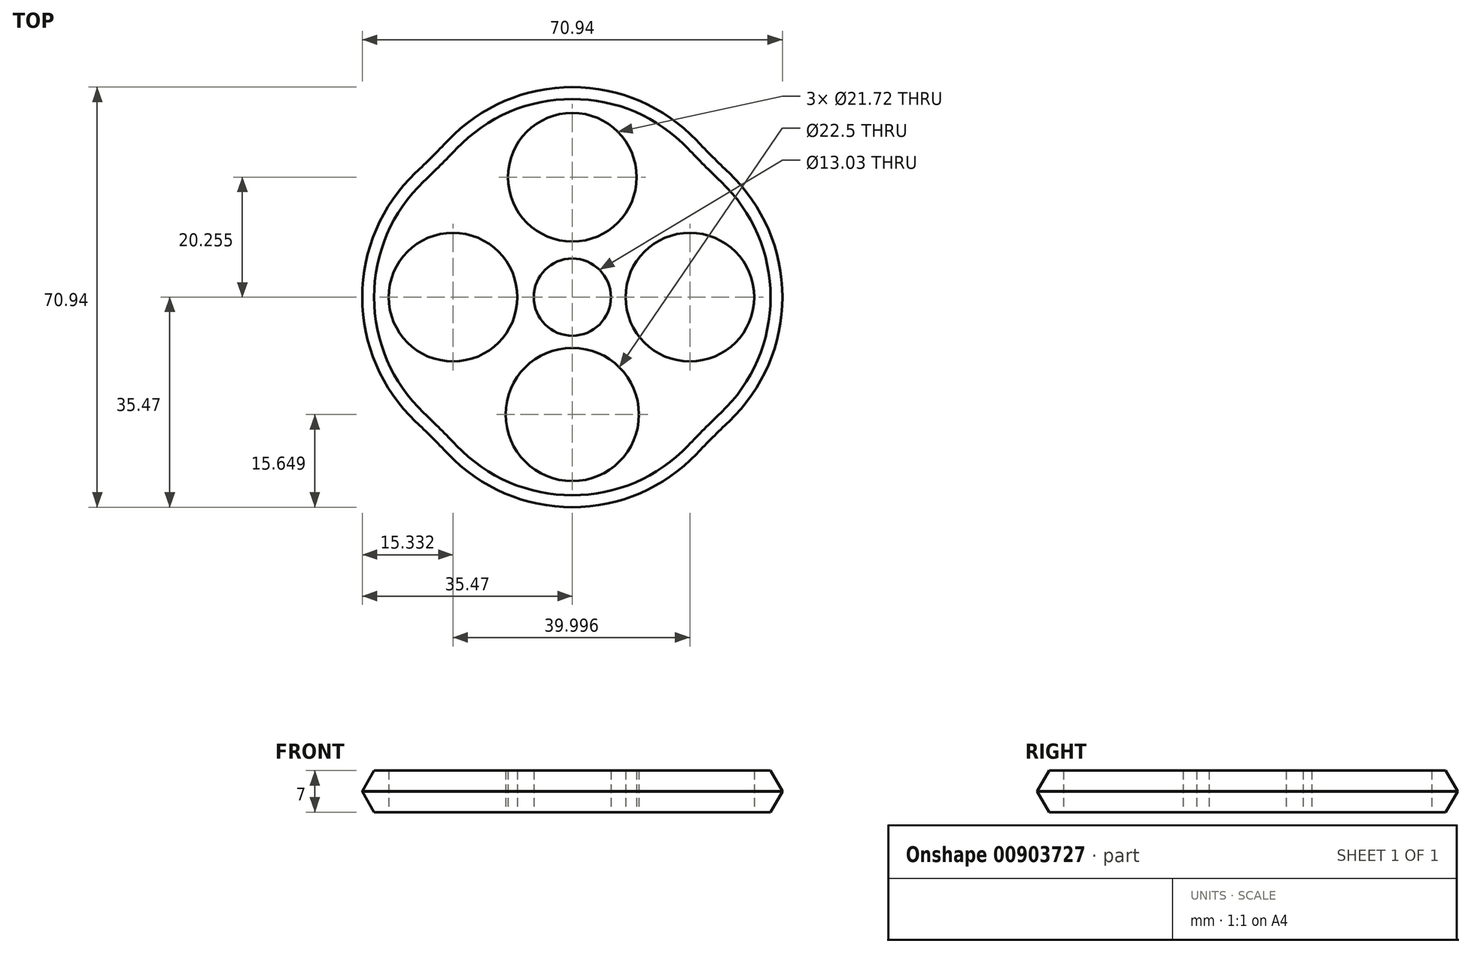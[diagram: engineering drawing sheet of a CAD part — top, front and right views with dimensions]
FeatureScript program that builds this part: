
annotation { "Feature Type Name" : "Feature", "Feature Type Description" : "" }
export const myFeature = defineFeature(function(context is Context, id is Id, definition is map)
    precondition{}
    {
        {
            var Q0;
            Q0=qCreatedBy(makeId("Top.planeOp"),FACE);
            var sketch = newSketch(context, id + "F0", { "sketchPlane" : qUnion([Q0])});
            skCircle(sketch, "E0", {"center": v(0, 0) * mm, "radius": 6.51 * mm});
            skCircle(sketch, "E1", {"center": v(0, 6.51) * mm, "radius": 28.95 * mm});
            skCircle(sketch, "E2", {"center": v(0, -6.51) * mm, "radius": 28.95 * mm});
            skCircle(sketch, "E3", {"center": v(-6.51, 0) * mm, "radius": 28.95 * mm});
            skCircle(sketch, "E4", {"center": v(6.51, 0) * mm, "radius": 28.95 * mm});
            skCircle(sketch, "E5", {"center": v(-20.14, 0) * mm, "radius": 10.86 * mm});
            skCircle(sketch, "E6", {"center": v(0, 20.25) * mm, "radius": 10.86 * mm});
            skCircle(sketch, "E7", {"center": v(19.86, 0) * mm, "radius": 10.86 * mm});
            skCircle(sketch, "E8", {"center": v(0, -19.82) * mm, "radius": 11.25 * mm});
            skSolve(sketch);
        }
        {
            var Q0;
            Q0=makeQuery(id+"F0.imprint","IMPRINT",FACE,{"disambiguationData":[TD([[makeQuery(id+"F0.imprint","IMPRINT",EDGE,{"derivedFrom":sQuery(id+"F0.wireOp",EDGE,"E0")}),-1.0]])]});
            var Q1;
            {var subQ0=sQuery(id+"F0.wireOp",EDGE,"E4");var subQ1=sQuery(id+"F0.wireOp",EDGE,"E2");var subQ2=makeQuery(id+"F0.imprint","INTERSECT",VERTEX,{"disambiguationData":[OD(1.0)],"derivedFrom":[subQ1,subQ0]});Q1=makeQuery(id+"F0.imprint","IMPRINT",FACE,{"disambiguationData":[TD([[makeQuery(id+"F0.imprint","IMPRINT",EDGE,{"disambiguationData":[TD([[subQ2,-1.0]])],"derivedFrom":subQ1}),1.0]])]});}
            var Q2;
            {var subQ5=sQuery(id+"F0.wireOp",EDGE,"E3");var subQ6=sQuery(id+"F0.wireOp",EDGE,"E1");var subQ7=makeQuery(id+"F0.imprint","INTERSECT",VERTEX,{"disambiguationData":[OD(0.0)],"derivedFrom":[subQ6,subQ5]});Q2=makeQuery(id+"F0.imprint","IMPRINT",FACE,{"disambiguationData":[TD([[makeQuery(id+"F0.imprint","IMPRINT",EDGE,{"disambiguationData":[TD([[subQ7,-1.0]])],"derivedFrom":subQ6}),1.0]])]});}
            var Q3;
            {var subQ0=sQuery(id+"F0.wireOp",EDGE,"E6");var subQ1=sQuery(id+"F0.wireOp",EDGE,"E2");var subQ2=makeQuery(id+"F0.imprint","INTERSECT",VERTEX,{"disambiguationData":[OD(1.0)],"derivedFrom":[subQ1,subQ0]});Q3=makeQuery(id+"F0.imprint","IMPRINT",FACE,{"disambiguationData":[TD([[makeQuery(id+"F0.imprint","IMPRINT",EDGE,{"disambiguationData":[TD([[subQ2,-1.0]])],"derivedFrom":subQ1}),-1.0]])]});}
            var Q4;
            {var subQ1=sQuery(id+"F0.wireOp",EDGE,"E1");var subQ8=sQuery(id+"F0.wireOp",EDGE,"E5");var subQ11=makeQuery(id+"F0.imprint","INTERSECT",VERTEX,{"disambiguationData":[OD(1.0)],"derivedFrom":[subQ1,subQ8]});Q4=makeQuery(id+"F0.imprint","IMPRINT",FACE,{"disambiguationData":[TD([[makeQuery(id+"F0.imprint","IMPRINT",EDGE,{"disambiguationData":[TD([[subQ11,-1.0]])],"derivedFrom":subQ1}),-1.0]])]});}
            var Q5;
            {var subQ0=sQuery(id+"F0.wireOp",EDGE,"E3");var subQ1=sQuery(id+"F0.wireOp",EDGE,"E2");var subQ2=makeQuery(id+"F0.imprint","INTERSECT",VERTEX,{"disambiguationData":[OD(0.0)],"derivedFrom":[subQ1,subQ0]});Q5=makeQuery(id+"F0.imprint","IMPRINT",FACE,{"disambiguationData":[TD([[makeQuery(id+"F0.imprint","IMPRINT",EDGE,{"disambiguationData":[TD([[subQ2,-1.0]])],"derivedFrom":subQ1}),1.0]])]});}
            var Q6;
            {var subQ0=sQuery(id+"F0.wireOp",EDGE,"E3");var subQ1=sQuery(id+"F0.wireOp",EDGE,"E1");var subQ2=makeQuery(id+"F0.imprint","INTERSECT",VERTEX,{"disambiguationData":[OD(0.0)],"derivedFrom":[subQ1,subQ0]});Q6=makeQuery(id+"F0.imprint","IMPRINT",FACE,{"disambiguationData":[TD([[makeQuery(id+"F0.imprint","IMPRINT",EDGE,{"disambiguationData":[TD([[subQ2,-1.0]])],"derivedFrom":subQ1}),-1.0]])]});}
            var Q7;
            {var subQ0=sQuery(id+"F0.wireOp",EDGE,"E3");var subQ1=sQuery(id+"F0.wireOp",EDGE,"E1");var subQ2=makeQuery(id+"F0.imprint","INTERSECT",VERTEX,{"disambiguationData":[OD(0.0)],"derivedFrom":[subQ1,subQ0]});Q7=makeQuery(id+"F0.imprint","IMPRINT",FACE,{"disambiguationData":[TD([[makeQuery(id+"F0.imprint","IMPRINT",EDGE,{"disambiguationData":[TD([[subQ2,1.0]])],"derivedFrom":subQ1}),1.0]])]});}
            var Q8;
            {var subQ7=sQuery(id+"F0.wireOp",EDGE,"E4");var subQ8=sQuery(id+"F0.wireOp",EDGE,"E1");var subQ9=makeQuery(id+"F0.imprint","INTERSECT",VERTEX,{"disambiguationData":[OD(0.0)],"derivedFrom":[subQ8,subQ7]});Q8=makeQuery(id+"F0.imprint","IMPRINT",FACE,{"disambiguationData":[TD([[makeQuery(id+"F0.imprint","IMPRINT",EDGE,{"disambiguationData":[TD([[subQ9,1.0]])],"derivedFrom":subQ8}),1.0]])]});}
            var Q9;
            {var subQ0=sQuery(id+"F0.wireOp",EDGE,"E3");var subQ1=sQuery(id+"F0.wireOp",EDGE,"E2");var subQ2=makeQuery(id+"F0.imprint","INTERSECT",VERTEX,{"disambiguationData":[OD(1.0)],"derivedFrom":[subQ1,subQ0]});Q9=makeQuery(id+"F0.imprint","IMPRINT",FACE,{"disambiguationData":[TD([[makeQuery(id+"F0.imprint","IMPRINT",EDGE,{"disambiguationData":[TD([[subQ2,-1.0]])],"derivedFrom":subQ1}),-1.0]])]});}
            var Q10;
            {var subQ0=sQuery(id+"F0.wireOp",EDGE,"E7");var subQ1=sQuery(id+"F0.wireOp",EDGE,"E2");var subQ2=makeQuery(id+"F0.imprint","INTERSECT",VERTEX,{"disambiguationData":[OD(1.0)],"derivedFrom":[subQ1,subQ0]});Q10=makeQuery(id+"F0.imprint","IMPRINT",FACE,{"disambiguationData":[TD([[makeQuery(id+"F0.imprint","IMPRINT",EDGE,{"disambiguationData":[TD([[subQ2,-1.0]])],"derivedFrom":subQ1}),1.0]])]});}
            var Q11;
            {var subQ0=sQuery(id+"F0.wireOp",EDGE,"E4");var subQ1=sQuery(id+"F0.wireOp",EDGE,"E1");var subQ2=makeQuery(id+"F0.imprint","INTERSECT",VERTEX,{"disambiguationData":[OD(0.0)],"derivedFrom":[subQ1,subQ0]});Q11=makeQuery(id+"F0.imprint","IMPRINT",FACE,{"disambiguationData":[TD([[makeQuery(id+"F0.imprint","IMPRINT",EDGE,{"disambiguationData":[TD([[subQ2,1.0]])],"derivedFrom":subQ1}),-1.0]])]});}
            var Q12;
            {var subQ0=sQuery(id+"F0.wireOp",EDGE,"E3");var subQ1=sQuery(id+"F0.wireOp",EDGE,"E1");var subQ2=makeQuery(id+"F0.imprint","INTERSECT",VERTEX,{"disambiguationData":[OD(1.0)],"derivedFrom":[subQ1,subQ0]});Q12=makeQuery(id+"F0.imprint","IMPRINT",FACE,{"disambiguationData":[TD([[makeQuery(id+"F0.imprint","IMPRINT",EDGE,{"disambiguationData":[TD([[subQ2,-1.0]])],"derivedFrom":subQ1}),1.0]])]});}
            var Q13;
            {var subQ0=sQuery(id+"F0.wireOp",EDGE,"E4");var subQ1=sQuery(id+"F0.wireOp",EDGE,"E1");var subQ2=makeQuery(id+"F0.imprint","INTERSECT",VERTEX,{"disambiguationData":[OD(1.0)],"derivedFrom":[subQ1,subQ0]});Q13=makeQuery(id+"F0.imprint","IMPRINT",FACE,{"disambiguationData":[TD([[makeQuery(id+"F0.imprint","IMPRINT",EDGE,{"disambiguationData":[TD([[subQ2,-1.0]])],"derivedFrom":subQ1}),-1.0]])]});}
            var Q14;
            {var subQ0=sQuery(id+"F0.wireOp",EDGE,"E5");var subQ1=sQuery(id+"F0.wireOp",EDGE,"E1");var subQ2=makeQuery(id+"F0.imprint","INTERSECT",VERTEX,{"disambiguationData":[OD(1.0)],"derivedFrom":[subQ1,subQ0]});Q14=makeQuery(id+"F0.imprint","IMPRINT",FACE,{"disambiguationData":[TD([[makeQuery(id+"F0.imprint","IMPRINT",EDGE,{"disambiguationData":[TD([[subQ2,-1.0]])],"derivedFrom":subQ1}),1.0]])]});}
            var Q15;
            {var subQ5=sQuery(id+"F0.wireOp",EDGE,"E3");var subQ6=sQuery(id+"F0.wireOp",EDGE,"E1");var subQ7=makeQuery(id+"F0.imprint","INTERSECT",VERTEX,{"disambiguationData":[OD(1.0)],"derivedFrom":[subQ6,subQ5]});Q15=makeQuery(id+"F0.imprint","IMPRINT",FACE,{"disambiguationData":[TD([[makeQuery(id+"F0.imprint","IMPRINT",EDGE,{"disambiguationData":[TD([[subQ7,-1.0]])],"derivedFrom":subQ6}),-1.0]])]});}
            var Q16;
            {var subQ0=sQuery(id+"F0.wireOp",EDGE,"E8");var subQ1=sQuery(id+"F0.wireOp",EDGE,"E1");var subQ2=makeQuery(id+"F0.imprint","INTERSECT",VERTEX,{"disambiguationData":[OD(1.0)],"derivedFrom":[subQ1,subQ0]});Q16=makeQuery(id+"F0.imprint","IMPRINT",FACE,{"disambiguationData":[TD([[makeQuery(id+"F0.imprint","IMPRINT",EDGE,{"disambiguationData":[TD([[subQ2,-1.0]])],"derivedFrom":subQ1}),-1.0]])]});}
            extrude(context, id + "F1", {"entities" : qUnion([Q0, Q1, Q2, Q3, Q4, Q5, Q6, Q7, Q8, Q9, Q10, Q11, Q12, Q13, Q14, Q15, Q16]), "depth" : 7 * mm, "offsetDistance" : 25 * mm});
        }
        {
            var Q0;
            Q0=makeQuery(id+"F1.opExtrude","SWEPT_EDGE",EDGE,{"disambiguationData":[OSD([sQuery(id+"F0.wireOp",EDGE,"E2"),sQuery(id+"F0.wireOp",EDGE,"E4")])]});
            var Q1;
            Q1=makeQuery(id+"F1.opExtrude","SWEPT_EDGE",EDGE,{"disambiguationData":[OSD([sQuery(id+"F0.wireOp",EDGE,"E1"),sQuery(id+"F0.wireOp",EDGE,"E4")])]});
            var Q2;
            Q2=makeQuery(id+"F1.opExtrude","SWEPT_EDGE",EDGE,{"disambiguationData":[OSD([sQuery(id+"F0.wireOp",EDGE,"E1"),sQuery(id+"F0.wireOp",EDGE,"E3")])]});
            var Q3;
            Q3=makeQuery(id+"F1.opExtrude","SWEPT_EDGE",EDGE,{"disambiguationData":[OSD([sQuery(id+"F0.wireOp",EDGE,"E2"),sQuery(id+"F0.wireOp",EDGE,"E3")])]});
            fillet(context, id + "F2", {"entities" : qUnion([Q0, Q1, Q2, Q3]), "radius" : 150 * mm, "tangentPropagation" : true, "allowEdgeOverflow" : false});
        }
        {
            var Q0;
            Q0=makeQuery(id+"F1.opExtrude","CAP_EDGE",EDGE,{"disambiguationData":[OSD([sQuery(id+"F0.wireOp",EDGE,"E3")])],"isStart":false});
            var Q1;
            Q1=makeQuery(id+"F1.opExtrude","CAP_EDGE",EDGE,{"disambiguationData":[OSD([sQuery(id+"F0.wireOp",EDGE,"E3")])],"isStart":true});
            chamfer(context, id + "F3", {"entities" : qUnion([Q0, Q1]), "chamferType" : ChamferType.OFFSET_ANGLE, "width" : 2 * mm, "oppositeDirection" : false, "angle" : 60 * degree, "tangentPropagation" : true});
        }
    });
